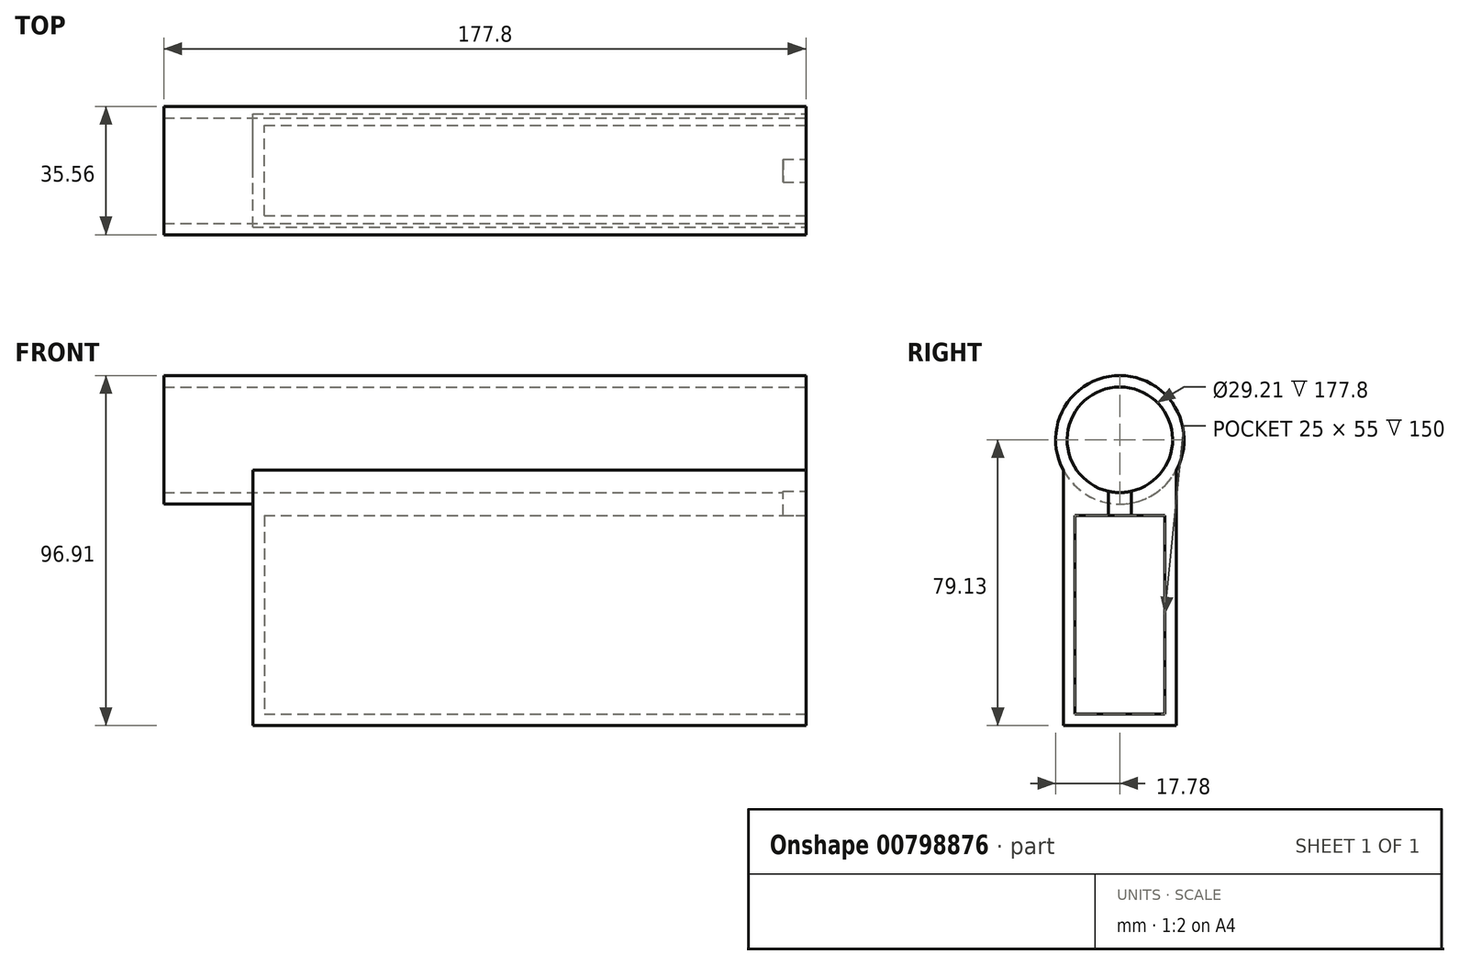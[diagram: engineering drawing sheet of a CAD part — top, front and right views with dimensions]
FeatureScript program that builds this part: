
annotation { "Feature Type Name" : "Feature", "Feature Type Description" : "" }
export const myFeature = defineFeature(function(context is Context, id is Id, definition is map)
    precondition{}
    {
        {
            var Q0;
            Q0=qCreatedBy(makeId("Right.planeOp"),FACE);
            var sketch = newSketch(context, id + "F0", { "sketchPlane" : qUnion([Q0])});
            skCircle(sketch, "E0", {"center": v(0, 0) * mm, "radius": 14.6 * mm});
            skCircle(sketch, "E1", {"center": v(0, 0) * mm, "radius": 17.78 * mm});
            skSolve(sketch);
        }
        {
            var Q0;
            Q0 = qSketchRegion(id + "F0", true);
            extrude(context, id + "F1", {"entities" : qUnion([Q0]), "oppositeDirection" : true, "depth" : 177.8 * mm, "offsetDistance" : 25.4 * mm});
        }
        {
            var Q0;
            Q0=qCreatedBy(makeId("Right.planeOp"),FACE);
            var sketch = newSketch(context, id + "F2", { "sketchPlane" : qUnion([Q0])});
            skLineSegment(sketch, "E2", {"start": v(0, 0) * mm, "end": v(0, -20.96) * mm, "construction": true});
            skLineSegment(sketch, "E3.bottom", {"start": v(-12.5, -20.96) * mm, "end": v(12.5, -20.95) * mm});
            skLineSegment(sketch, "E3.top", {"start": v(-12.5, -75.95) * mm, "end": v(12.5, -75.95) * mm});
            skLineSegment(sketch, "E3.left", {"start": v(-12.5, -20.96) * mm, "end": v(-12.5, -75.95) * mm});
            skLineSegment(sketch, "E3.right", {"start": v(12.5, -20.95) * mm, "end": v(12.5, -75.95) * mm});
            skLineSegment(sketch, "E4.0", {"start": v(-15.68, -17.78) * mm, "end": v(-15.68, -79.13) * mm});
            skLineSegment(sketch, "E4.1", {"start": v(-15.68, -17.78) * mm, "end": v(15.68, -17.78) * mm});
            skLineSegment(sketch, "E4.2", {"start": v(15.68, -17.78) * mm, "end": v(15.68, -79.13) * mm});
            skLineSegment(sketch, "E4.3", {"start": v(-15.68, -79.13) * mm, "end": v(15.68, -79.13) * mm});
            skLineSegment(sketch, "E5", {"start": v(-15.68, -17.78) * mm, "end": v(-15.68, -8.4) * mm});
            skLineSegment(sketch, "E6", {"start": v(15.68, -17.78) * mm, "end": v(15.68, -8.4) * mm});
            skArc(sketch, "E7", {"start": v(-15.68, -8.4) * mm, "mid": v(0, -17.78) * mm, "end": v(15.68, -8.4) * mm});
            skSolve(sketch);
        }
        {
            var Q0;
            Q0 = qSketchRegion(id + "F2", true);
            extrude(context, id + "F3", {"entities" : qUnion([Q0]), "operationType" : NewBodyOperationType.ADD, "oppositeDirection" : true, "depth" : 150 * mm, "offsetDistance" : 25.4 * mm});
        }
        {
            var Q0;
            Q0=makeQuery(id+"F3.opExtrude","CAP_FACE",FACE,{"disambiguationData":[OSD([sQuery(id+"F2.wireOp",EDGE,"E3.bottom"),sQuery(id+"F2.wireOp",EDGE,"E3.top"),sQuery(id+"F2.wireOp",EDGE,"E3.left"),sQuery(id+"F2.wireOp",EDGE,"E3.right"),sQuery(id+"F2.wireOp",EDGE,"E4.0"),sQuery(id+"F2.wireOp",EDGE,"E4.2"),sQuery(id+"F2.wireOp",EDGE,"E4.3"),sQuery(id+"F2.wireOp",EDGE,"E5"),sQuery(id+"F2.wireOp",EDGE,"E6"),sQuery(id+"F2.wireOp",EDGE,"E7")])],"isStart":false});
            var sketch = newSketch(context, id + "F4", { "sketchPlane" : qUnion([Q0])});
            skPoint(sketch, "E8.oppositeSnap0", {"position": v(0, -17.78) * mm});
            skPoint(sketch, "E8.oppositeSnap1", {"position": v(15.68, -43.76) * mm});
            skLineSegment(sketch, "E8.bottom", {"start": v(-15.68, -79.13) * mm, "end": v(15.68, -79.13) * mm});
            skLineSegment(sketch, "E8.top", {"start": v(-15.68, -17.78) * mm, "end": v(15.68, -17.78) * mm});
            skLineSegment(sketch, "E8.left", {"start": v(-15.68, -79.13) * mm, "end": v(-15.68, -17.78) * mm});
            skLineSegment(sketch, "E8.right", {"start": v(15.68, -79.13) * mm, "end": v(15.68, -17.78) * mm});
            skArc(sketch, "E9", {"start": v(-15.68, -8.4) * mm, "mid": v(0, -17.78) * mm, "end": v(15.68, -8.4) * mm});
            skLineSegment(sketch, "E10", {"start": v(-15.68, -8.4) * mm, "end": v(-15.68, -17.78) * mm});
            skLineSegment(sketch, "E11", {"start": v(15.68, -8.4) * mm, "end": v(15.68, -17.78) * mm});
            skSolve(sketch);
        }
        {
            var Q0;
            Q0 = qSketchRegion(id + "F4", true);
            extrude(context, id + "F5", {"entities" : qUnion([Q0]), "operationType" : NewBodyOperationType.ADD, "depth" : 3.17 * mm, "offsetDistance" : 25.4 * mm});
        }
        {
            var Q0;
            Q0=qCreatedBy(makeId("Right.planeOp"),FACE);
            var sketch = newSketch(context, id + "F6", { "sketchPlane" : qUnion([Q0])});
            skLineSegment(sketch, "E12.bottom", {"start": v(3.18, -24.9) * mm, "end": v(-3.17, -24.9) * mm});
            skLineSegment(sketch, "E12.top", {"start": v(3.18, -11.23) * mm, "end": v(-3.17, -11.23) * mm});
            skLineSegment(sketch, "E12.left", {"start": v(3.18, -24.9) * mm, "end": v(3.18, -11.23) * mm});
            skLineSegment(sketch, "E12.right", {"start": v(-3.18, -24.9) * mm, "end": v(-3.18, -11.23) * mm});
            skPoint(sketch, "E12.middle", {"position": v(0, -18.07) * mm});
            skSolve(sketch);
        }
        {
            var Q0;
            Q0=makeQuery(id+"F6.imprint","IMPRINT",FACE,{"disambiguationData":[TD([[makeQuery(id+"F6.imprint","IMPRINT",EDGE,{"derivedFrom":sQuery(id+"F6.wireOp",EDGE,"E12.bottom")}),-1.0]])]});
            extrude(context, id + "F7", {"entities" : qUnion([Q0]), "operationType" : NewBodyOperationType.REMOVE, "oppositeDirection" : true, "depth" : 6.35 * mm, "offsetDistance" : 25.4 * mm});
        }
    });
